# Revit family: 0044074 Sylvania Lighting Fixture OPTIX S 1200 MPO DI HO 4000K D+EM WHITE
name_source: partatom
category: Lighting Fixtures
revit_build: Autodesk Revit 2016 (Build: 20150220_1215(x64)
units: mm (PartAtom-declared; Revit-internal decimal feet)

## family parameters
Cut with Voids When Loaded = No
Host = Face
Light Source = Yes
OmniClass Number = 23.80.70.00
OmniClass Title = Lighting
Part Type = Normal
Room Calculation Point = No
Round Connector Dimension = Use Diameter
Shared = No

## types (1)
- 0044074 OPTIX S 1200 MPO D/I HO 4K D+EM WHITE
    Apparent Load = 47 VA
    Assembly Code = D5020200
    AssetType = Fixed
    ClassificationName = Uniclass2015
    ClassificationValue = EF_70_80
    Color Filter = 16777215
    Cost = 0 $
    Default Elevation = 1219 mm
    Description = OPTIX S 1200 MPO D/I HO 4K D+EM WHITE is a high efficacy low glare surface or suspended LED Linear luminaire with Micro Prismatic Optic, with direct/indirect light distribution, luminaire dimensions: 1200x200x50mm, Sylvania White body colour (RAL9016), IP20, IK07, DALI Dimmable, 3hr maintained emergency version, low LED flicker (+/-5%), Neutral White (4000K) LED Colour Temperature, 5770lm luminous flux, 47W power consumption, 122lm/W system efficacy, CRI>80, SDCM 3 (3-step MacAdam ellipse) LED Colour Consistency, UGR<18, Luminance at 65° < 3000 cd/m2, lumen maintenance: L90B50 at 60000h, photobiological safety risk group 1. Electrical protection Class I.
    Dimming Lamp Color Temperature Shift = <None>
    DocumentationLiterature = http://www.sylvania-lighting.com
    DurationUnit = hours
    ElectricShockClassification = 122
    Emit Shape Visible in Rendering = No
    Emit from Circle Diameter = 610 mm
    ExpectedLife = 50000
    Height = 50 mm  [stored 0.164042 ft]
    IfcExportAs = Class I
    IfcExportType = IfcLightFixtureType
    ImpactProtectionIndex = IfcLightFixtureType
    IngressProtection = IfcLightFixtureType
    InputNominalFrequency = 4000
    InputVoltage = 0
    LampColourRenderingIndex = 16500
    LampColourTemperature = LED
    LampMacAdamStep = 80
    LampNominalLuminous = 4000 K
    Length = 1188 mm  [stored 3.89764 ft]
    Lens Width = 135 mm  [stored 0.442913 ft]
    LightOutputRatio = LED
    LuminaireType = 0
    ManufacturerName = 122 lm/W
    Material = Feilo Sylvania
    Material_1_FEILO = <By Category>
    Material_2_FEILO = <By Category>
    Material_3_FEILO = <By Category>
    Material_4_FEILO = <By Category>
    Model = OPTIX S 1200 MPO D/I HO 4000K D+EM WHITE
    ModelNumber = 0044074
    ModelReference = OPTIX S 1200 MPO D/I HO 4000K D+EM WHITE
    Name = OPTIX S 1200 MPO D/I HO 4000K D+EM WHITE
    NominalDepth = 0 mm  [stored 0 ft]
    NominalHeight = 0 mm  [stored 0 ft]
    NominalLength = 200 mm  [stored 0.656168 ft]
    Photometric Web File = 0044074.ies
    PowerConsumption = Lighting
    PowerFactor = 0
    Tilt Angle = 90.00°
    Type Image = <None>
    TypeName = OPTIX S 1200 MPO D/I HO 4000K D+EM WHITE
    URL = 0.98
    Voltage = 0 V
    WarrantyDescription = http://www.sylvania-lighting.com
    Width = 200 mm  [stored 0.656168 ft]
    full length = 1200 mm  [stored 3.93701 ft]
    lens width = 1135 mm  [stored 3.72375 ft]
    spacer centres = 1000 mm  [stored 3.28084 ft]
    spacer height = 5 mm  [stored 0.0164042 ft]

note: [stored X ft] marks values corroborated as IEEE doubles in the binary element streams (Revit-internal decimal feet)

## geometry (parser evidence)
native form markers: Sweep x2
no freeform markers — native parametric forms only
